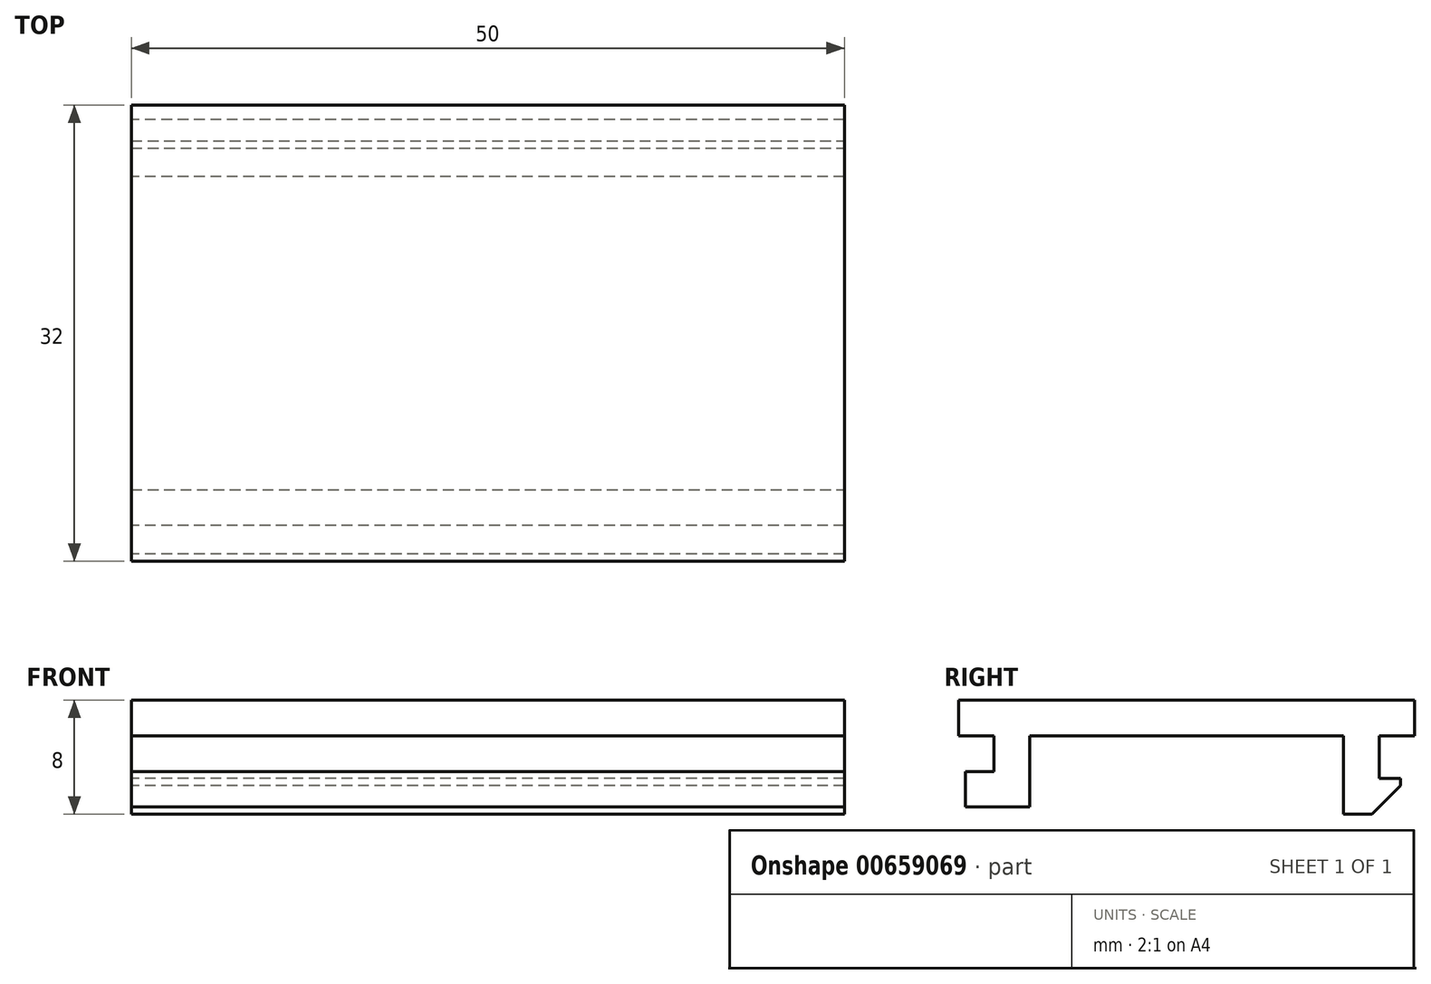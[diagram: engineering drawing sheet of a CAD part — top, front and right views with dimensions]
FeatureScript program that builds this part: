
annotation { "Feature Type Name" : "Feature", "Feature Type Description" : "" }
export const myFeature = defineFeature(function(context is Context, id is Id, definition is map)
    precondition{}
    {
        {
            var Q0;
            Q0=qCreatedBy(makeId("Top.planeOp"),FACE);
            var sketch = newSketch(context, id + "F0", { "sketchPlane" : qUnion([Q0])});
            skLineSegment(sketch, "E0.bottom", {"start": v(25, 16) * mm, "end": v(-25, 16) * mm});
            skLineSegment(sketch, "E0.top", {"start": v(25, -16) * mm, "end": v(-25, -16) * mm});
            skLineSegment(sketch, "E0.left", {"start": v(25, 16) * mm, "end": v(25, -16) * mm});
            skLineSegment(sketch, "E0.right", {"start": v(-25, 16) * mm, "end": v(-25, -16) * mm});
            skPoint(sketch, "E0.middle", {"position": v(0, 0) * mm});
            skLineSegment(sketch, "E1", {"start": v(-25, 13.5) * mm, "end": v(25, 13.5) * mm});
            skLineSegment(sketch, "E2", {"start": v(25, -13.5) * mm, "end": v(-25, -13.5) * mm});
            skLineSegment(sketch, "E3", {"start": v(-25, -11) * mm, "end": v(25, -11) * mm});
            skLineSegment(sketch, "E4", {"start": v(25, 11) * mm, "end": v(-25, 11) * mm});
            skSolve(sketch);
        }
        {
            var Q0;
            Q0 = qSketchRegion(id + "F0", true);
            extrude(context, id + "F1", {"entities" : qUnion([Q0]), "depth" : 2.5 * mm, "offsetDistance" : 25 * mm});
        }
        {
            var Q0;
            {var subQ0=sQuery(id+"F0.wireOp",EDGE,"E2");Q0=makeQuery(id+"F0.imprint","IMPRINT",FACE,{"disambiguationData":[TD([[makeQuery(id+"F0.imprint","IMPRINT",EDGE,{"derivedFrom":subQ0}),-1.0]])]});}
            extrude(context, id + "F2", {"entities" : qUnion([Q0]), "operationType" : NewBodyOperationType.ADD, "depth" : -5 * mm, "offsetDistance" : 25 * mm});
        }
        {
            var Q0;
            Q0=makeQuery(id+"F2.opExtrude","SWEPT_FACE",FACE,{"disambiguationData":[OSD([sQuery(id+"F0.wireOp",EDGE,"E2")])]});
            var sketch = newSketch(context, id + "F3", { "sketchPlane" : qUnion([Q0])});
            skLineSegment(sketch, "E5", {"start": v(-25, -2.5) * mm, "end": v(25, -2.5) * mm});
            skSolve(sketch);
        }
        {
            var Q0;
            {var subQ0=sQuery(id+"F3.wireOp",EDGE,"E5");Q0=makeQuery(id+"F3.imprint","IMPRINT",FACE,{"disambiguationData":[TD([[makeQuery(id+"F3.imprint","IMPRINT",EDGE,{"derivedFrom":subQ0}),-1.0]])]});}
            extrude(context, id + "F4", {"entities" : qUnion([Q0]), "operationType" : NewBodyOperationType.ADD, "depth" : 2 * mm, "offsetDistance" : 25 * mm});
        }
        {
            var Q0;
            {var subQ0=sQuery(id+"F0.wireOp",EDGE,"E1");Q0=makeQuery(id+"F0.imprint","IMPRINT",FACE,{"disambiguationData":[TD([[makeQuery(id+"F0.imprint","IMPRINT",EDGE,{"derivedFrom":subQ0}),-1.0]])]});}
            extrude(context, id + "F5", {"entities" : qUnion([Q0]), "operationType" : NewBodyOperationType.ADD, "depth" : -5.5 * mm, "offsetDistance" : 25 * mm});
        }
        {
            var Q0;
            Q0=makeQuery(id+"F5.opExtrude","SWEPT_FACE",FACE,{"disambiguationData":[OSD([sQuery(id+"F0.wireOp",EDGE,"E1")])]});
            var sketch = newSketch(context, id + "F6", { "sketchPlane" : qUnion([Q0])});
            skLineSegment(sketch, "E6", {"start": v(-25, -3) * mm, "end": v(25, -3) * mm});
            skSolve(sketch);
        }
        {
            var Q0;
            {var subQ0=sQuery(id+"F6.wireOp",EDGE,"E6");Q0=makeQuery(id+"F6.imprint","IMPRINT",FACE,{"disambiguationData":[TD([[makeQuery(id+"F6.imprint","IMPRINT",EDGE,{"derivedFrom":subQ0}),-1.0]])]});}
            extrude(context, id + "F7", {"entities" : qUnion([Q0]), "operationType" : NewBodyOperationType.ADD, "depth" : 1.5 * mm, "offsetDistance" : 25 * mm});
        }
        {
            var Q0;
            Q0=makeQuery(id+"F7.opExtrude","CAP_EDGE",EDGE,{"disambiguationData":[OSD([sQuery(id+"F0.wireOp",EDGE,"E1")])],"isStart":false});
            chamfer(context, id + "F8", {"entities" : qUnion([Q0]), "width" : 2 * mm, "tangentPropagation" : true});
        }
    });
